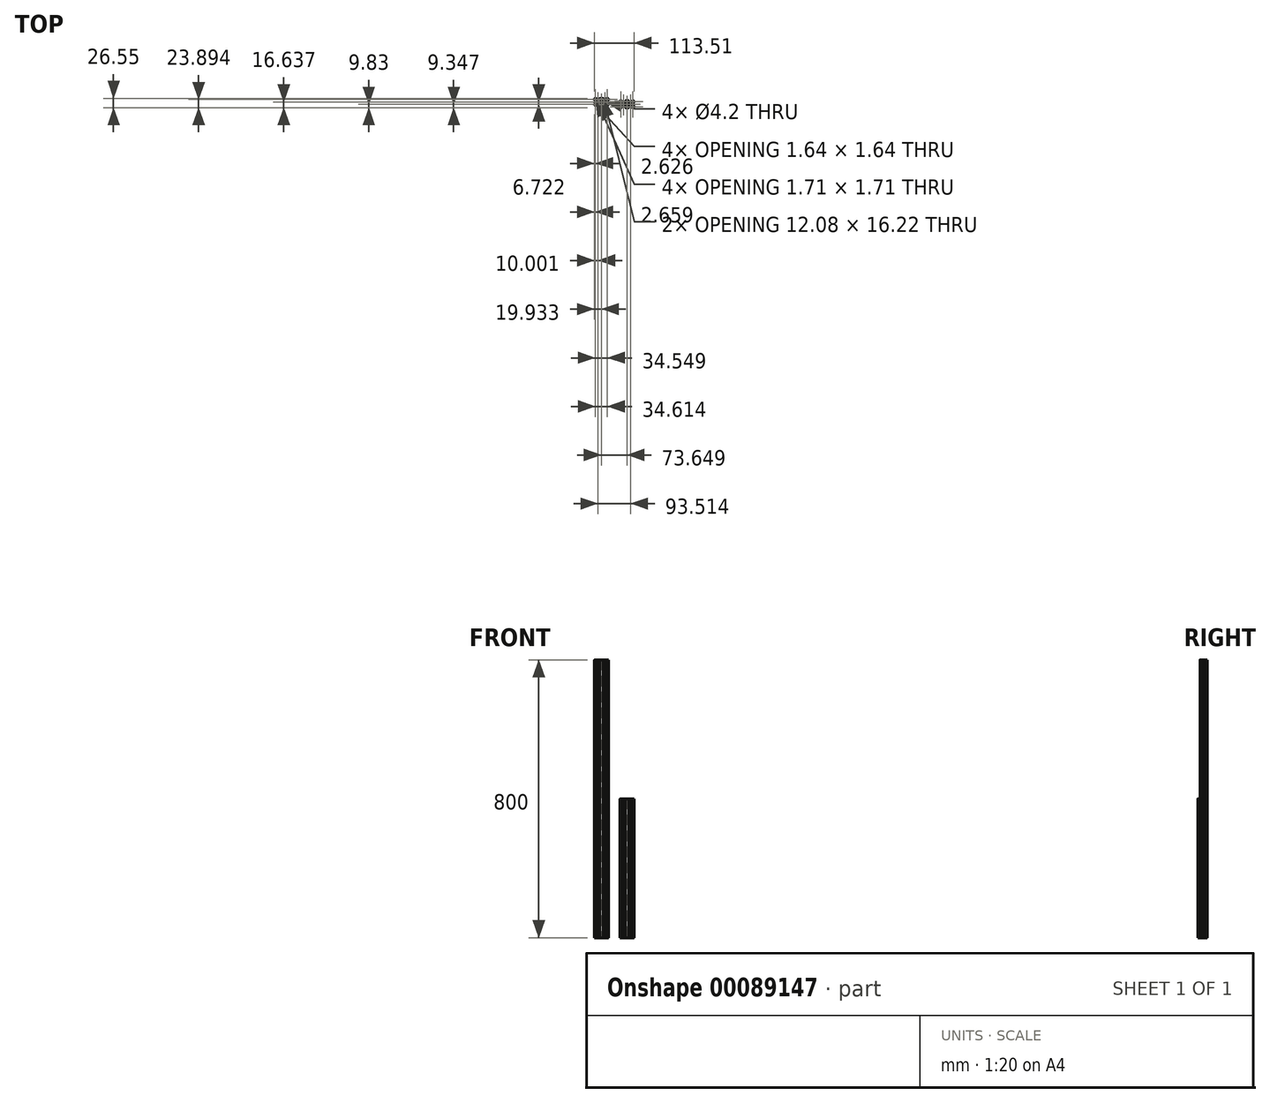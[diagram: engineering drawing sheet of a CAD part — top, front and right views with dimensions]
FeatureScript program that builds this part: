
annotation { "Feature Type Name" : "Feature", "Feature Type Description" : "" }
export const myFeature = defineFeature(function(context is Context, id is Id, definition is map)
    precondition{}
    {
        {
            var Q0;
            Q0=qCreatedBy(makeId("Top.planeOp"),FACE);
            var sketch = newSketch(context, id + "F0", { "sketchPlane" : qUnion([Q0])});
            skLineSegment(sketch, "E0.bottom", {"start": v(1.27, 0.17) * mm, "end": v(4.85, 0.17) * mm});
            skLineSegment(sketch, "E0.top", {"start": v(1.27, 20) * mm, "end": v(4.9, 20) * mm});
            skLineSegment(sketch, "E0.left", {"start": v(0, 1.44) * mm, "end": v(0, 5.01) * mm});
            skLineSegment(sketch, "E1.bottom", {"start": v(17.2, 18.2) * mm, "end": v(19.93, 18.2) * mm});
            skLineSegment(sketch, "E1.top", {"start": v(17.2, 1.97) * mm, "end": v(19.93, 1.97) * mm});
            skLineSegment(sketch, "E1.left", {"start": v(17.2, 18.2) * mm, "end": v(17.2, 16.24) * mm});
            skLineSegment(sketch, "E2.left", {"start": v(13.9, 12.92) * mm, "end": v(13.9, 7.24) * mm});
            skLineSegment(sketch, "E3", {"start": v(13.9, 12.92) * mm, "end": v(17.2, 16.24) * mm});
            skLineSegment(sketch, "E4", {"start": v(13.9, 7.24) * mm, "end": v(17.2, 3.93) * mm});
            skLineSegment(sketch, "E5.top", {"start": v(7.17, 13.95) * mm, "end": v(12.85, 13.95) * mm});
            skLineSegment(sketch, "E6", {"start": v(4.58, 18.2) * mm, "end": v(4.58, 16.55) * mm});
            skLineSegment(sketch, "E7", {"start": v(15.46, 16.56) * mm, "end": v(15.46, 18.2) * mm});
            skLineSegment(sketch, "E8", {"start": v(4.58, 16.55) * mm, "end": v(7.17, 13.95) * mm});
            skLineSegment(sketch, "E9", {"start": v(12.85, 13.95) * mm, "end": v(15.46, 16.56) * mm});
            skLineSegment(sketch, "E10", {"start": v(4.58, 18.2) * mm, "end": v(6.7, 18.2) * mm});
            skLineSegment(sketch, "E11.trimOffspring", {"start": v(17.2, 3.93) * mm, "end": v(17.2, 1.97) * mm});
            skLineSegment(sketch, "E12", {"start": v(19.93, 20) * mm, "end": v(19.93, 0.17) * mm, "construction": true});
            skLineSegment(sketch, "E13", {"start": v(1.8, 15.55) * mm, "end": v(1.8, 13.42) * mm});
            skLineSegment(sketch, "E14", {"start": v(1.8, 4.68) * mm, "end": v(3.45, 4.68) * mm});
            skLineSegment(sketch, "E15", {"start": v(3.45, 4.68) * mm, "end": v(6.05, 7.27) * mm});
            skLineSegment(sketch, "E16", {"start": v(6.05, 7.27) * mm, "end": v(6.05, 12.96) * mm});
            skLineSegment(sketch, "E17", {"start": v(6.05, 12.96) * mm, "end": v(3.45, 15.55) * mm});
            skLineSegment(sketch, "E18", {"start": v(3.45, 15.55) * mm, "end": v(1.8, 15.55) * mm});
            skLineSegment(sketch, "E19", {"start": v(7.1, 6.21) * mm, "end": v(12.8, 6.21) * mm});
            skLineSegment(sketch, "E20", {"start": v(12.8, 6.21) * mm, "end": v(15.38, 3.63) * mm});
            skLineSegment(sketch, "E21", {"start": v(15.38, 3.63) * mm, "end": v(15.38, 1.97) * mm});
            skLineSegment(sketch, "E22", {"start": v(15.38, 1.97) * mm, "end": v(13.26, 1.97) * mm});
            skLineSegment(sketch, "E23", {"start": v(4.51, 1.97) * mm, "end": v(4.51, 3.62) * mm});
            skLineSegment(sketch, "E24", {"start": v(4.51, 3.62) * mm, "end": v(7.1, 6.21) * mm});
            skLineSegment(sketch, "E25", {"start": v(1.8, 3.62) * mm, "end": v(2.34, 3.62) * mm});
            skLineSegment(sketch, "E26", {"start": v(2.34, 3.62) * mm, "end": v(3.45, 2.51) * mm});
            skLineSegment(sketch, "E27", {"start": v(3.45, 2.51) * mm, "end": v(3.45, 1.97) * mm});
            skLineSegment(sketch, "E28", {"start": v(3.45, 1.97) * mm, "end": v(1.8, 1.97) * mm});
            skLineSegment(sketch, "E29", {"start": v(1.8, 3.62) * mm, "end": v(1.8, 1.97) * mm});
            skPoint(sketch, "E30.endSnap0", {"position": v(10.01, 13.95) * mm});
            skCircle(sketch, "E31", {"center": v(10, 10) * mm, "radius": 2.1 * mm});
            skLineSegment(sketch, "E32", {"start": v(1.8, 18.2) * mm, "end": v(3.51, 18.2) * mm});
            skLineSegment(sketch, "E33", {"start": v(3.51, 18.2) * mm, "end": v(3.51, 17.66) * mm});
            skLineSegment(sketch, "E34", {"start": v(3.51, 17.66) * mm, "end": v(2.34, 16.49) * mm});
            skLineSegment(sketch, "E35", {"start": v(2.34, 16.49) * mm, "end": v(1.8, 16.49) * mm});
            skLineSegment(sketch, "E36", {"start": v(1.8, 16.49) * mm, "end": v(1.8, 18.2) * mm});
            skArc(sketch, "E37.filletArc", {"start": v(0, 1.44) * mm, "mid": v(0.37, 0.54) * mm, "end": v(1.27, 0.17) * mm});
            skArc(sketch, "E38.filletArc", {"start": v(1.27, 20) * mm, "mid": v(0.37, 19.63) * mm, "end": v(0, 18.73) * mm});
            skLineSegment(sketch, "E39", {"start": v(4.9, 20) * mm, "end": v(6.7, 18.2) * mm});
            skLineSegment(sketch, "E40", {"start": v(10.01, 13.95) * mm, "end": v(10.01, 14.9) * mm, "construction": true});
            skLineSegment(sketch, "E41", {"start": v(10.01, 14.9) * mm, "end": v(10.01, 20) * mm, "construction": true});
            skLineSegment(sketch, "E42", {"start": v(10.01, 21.22) * mm, "end": v(10.01, 20) * mm, "construction": true});
            skLineSegment(sketch, "E43.trimOffspring", {"start": v(15.12, 20) * mm, "end": v(19.93, 20) * mm});
            skLineSegment(sketch, "E44.trimOffspring", {"start": v(13.32, 18.2) * mm, "end": v(15.46, 18.2) * mm});
            skPoint(sketch, "E45.orphan", {"position": v(3.68, 21.22) * mm});
            skPoint(sketch, "E46.orphan", {"position": v(16.35, 21.22) * mm});
            skLineSegment(sketch, "E47", {"start": v(13.32, 18.2) * mm, "end": v(15.12, 20) * mm});
            skLineSegment(sketch, "E48", {"start": v(1.8, 13.42) * mm, "end": v(0, 15.22) * mm});
            skLineSegment(sketch, "E49", {"start": v(0, 5.01) * mm, "end": v(1.8, 6.82) * mm});
            skLineSegment(sketch, "E50.trimOffspring", {"start": v(0, 15.22) * mm, "end": v(0, 18.73) * mm});
            skLineSegment(sketch, "E51.trimOffspring", {"start": v(1.8, 6.82) * mm, "end": v(1.8, 4.68) * mm});
            skLineSegment(sketch, "E52", {"start": v(15.06, 0.17) * mm, "end": v(13.26, 1.97) * mm});
            skLineSegment(sketch, "E53", {"start": v(6.65, 1.97) * mm, "end": v(4.85, 0.17) * mm});
            skLineSegment(sketch, "E54.trimOffspring", {"start": v(15.06, 0.17) * mm, "end": v(19.93, 0.17) * mm});
            skLineSegment(sketch, "E55.trimOffspring", {"start": v(6.65, 1.97) * mm, "end": v(4.51, 1.97) * mm});
            skLineSegment(sketch, "E56.MirrorCS", {"start": v(36.35, 18.2) * mm, "end": v(36.35, 17.66) * mm});
            skLineSegment(sketch, "E57.MirrorCS", {"start": v(38.06, 3.62) * mm, "end": v(37.52, 3.62) * mm});
            skLineSegment(sketch, "E58.MirrorCS", {"start": v(36.42, 2.51) * mm, "end": v(36.42, 1.97) * mm});
            skLineSegment(sketch, "E59.MirrorCS", {"start": v(37.53, 16.49) * mm, "end": v(38.06, 16.49) * mm});
            skLineSegment(sketch, "E60.MirrorCS", {"start": v(29.85, 13.95) * mm, "end": v(29.85, 14.9) * mm, "construction": true});
            skLineSegment(sketch, "E61.MirrorCS", {"start": v(24.8, 0.17) * mm, "end": v(26.6, 1.97) * mm});
            skLineSegment(sketch, "E62.MirrorCS", {"start": v(35.29, 18.2) * mm, "end": v(35.29, 16.55) * mm});
            skLineSegment(sketch, "E63.MirrorCS", {"start": v(36.42, 1.97) * mm, "end": v(38.06, 1.97) * mm});
            skLineSegment(sketch, "E64.MirrorCS", {"start": v(24.48, 3.63) * mm, "end": v(24.48, 1.97) * mm});
            skLineSegment(sketch, "E65.MirrorCS", {"start": v(35.35, 1.97) * mm, "end": v(35.35, 3.62) * mm});
            skLineSegment(sketch, "E66.MirrorCS", {"start": v(22.66, 18.2) * mm, "end": v(22.66, 16.24) * mm});
            skLineSegment(sketch, "E67.MirrorCS", {"start": v(38.06, 16.49) * mm, "end": v(38.06, 18.2) * mm});
            skLineSegment(sketch, "E68.MirrorCS", {"start": v(24.4, 16.56) * mm, "end": v(24.4, 18.2) * mm});
            skLineSegment(sketch, "E69.MirrorCS", {"start": v(37.52, 3.62) * mm, "end": v(36.42, 2.51) * mm});
            skLineSegment(sketch, "E70.MirrorCS", {"start": v(38.06, 3.62) * mm, "end": v(38.06, 1.97) * mm});
            skLineSegment(sketch, "E71.MirrorCS", {"start": v(36.35, 17.66) * mm, "end": v(37.53, 16.49) * mm});
            skLineSegment(sketch, "E72.MirrorCS", {"start": v(32.76, 6.21) * mm, "end": v(27.06, 6.21) * mm});
            skLineSegment(sketch, "E73.MirrorCS", {"start": v(34.96, 20) * mm, "end": v(33.16, 18.2) * mm});
            skLineSegment(sketch, "E74.MirrorCS", {"start": v(38.06, 4.68) * mm, "end": v(36.41, 4.68) * mm});
            skLineSegment(sketch, "E75.MirrorCS", {"start": v(26.54, 18.2) * mm, "end": v(24.74, 20) * mm});
            skLineSegment(sketch, "E76.MirrorCS", {"start": v(24.74, 20) * mm, "end": v(19.93, 20) * mm});
            skLineSegment(sketch, "E77.MirrorCS", {"start": v(29.85, 14.9) * mm, "end": v(29.85, 20) * mm, "construction": true});
            skLineSegment(sketch, "E78.MirrorCS", {"start": v(33.21, 1.97) * mm, "end": v(35.02, 0.17) * mm});
            skLineSegment(sketch, "E79.MirrorCS", {"start": v(32.7, 13.95) * mm, "end": v(27.01, 13.95) * mm});
            skLineSegment(sketch, "E80.MirrorCS", {"start": v(22.66, 3.93) * mm, "end": v(22.66, 1.97) * mm});
            skLineSegment(sketch, "E81.MirrorCS", {"start": v(36.41, 4.68) * mm, "end": v(33.82, 7.27) * mm});
            skLineSegment(sketch, "E82.MirrorCS", {"start": v(29.85, 21.22) * mm, "end": v(29.85, 20) * mm, "construction": true});
            skLineSegment(sketch, "E83.MirrorCS", {"start": v(33.21, 1.97) * mm, "end": v(35.35, 1.97) * mm});
            skLineSegment(sketch, "E84.MirrorCS", {"start": v(25.97, 12.92) * mm, "end": v(25.97, 7.24) * mm});
            skLineSegment(sketch, "E85.MirrorCS", {"start": v(35.29, 18.2) * mm, "end": v(33.16, 18.2) * mm});
            skLineSegment(sketch, "E86.MirrorCS", {"start": v(27.01, 13.95) * mm, "end": v(24.4, 16.56) * mm});
            skCircle(sketch, "E87.MirrorC", {"center": v(29.86, 10) * mm, "radius": 2.1 * mm});
            skLineSegment(sketch, "E88.MirrorCS", {"start": v(38.06, 13.42) * mm, "end": v(39.86, 15.22) * mm});
            skLineSegment(sketch, "E89.MirrorCS", {"start": v(22.66, 1.97) * mm, "end": v(19.93, 1.97) * mm});
            skLineSegment(sketch, "E90.MirrorCS", {"start": v(38.6, 0.17) * mm, "end": v(35.02, 0.17) * mm});
            skLineSegment(sketch, "E91.MirrorCS", {"start": v(38.06, 18.2) * mm, "end": v(36.35, 18.2) * mm});
            skLineSegment(sketch, "E92.MirrorCS", {"start": v(33.82, 7.27) * mm, "end": v(33.82, 12.96) * mm});
            skPoint(sketch, "E93.MirrorP", {"position": v(36.18, 21.22) * mm});
            skLineSegment(sketch, "E94.MirrorCS", {"start": v(39.86, 1.44) * mm, "end": v(39.86, 5.01) * mm});
            skLineSegment(sketch, "E95.MirrorCS", {"start": v(24.48, 1.97) * mm, "end": v(26.6, 1.97) * mm});
            skLineSegment(sketch, "E96.MirrorCS", {"start": v(36.41, 15.55) * mm, "end": v(38.06, 15.55) * mm});
            skArc(sketch, "E97.MirrorCS", {"start": v(38.6, 20) * mm, "mid": v(39.5, 19.63) * mm, "end": v(39.86, 18.73) * mm});
            skPoint(sketch, "E98.MirrorP", {"position": v(29.85, 13.95) * mm});
            skPoint(sketch, "E99.MirrorP", {"position": v(23.52, 21.22) * mm});
            skLineSegment(sketch, "E100.MirrorCS", {"start": v(38.06, 6.82) * mm, "end": v(38.06, 4.68) * mm});
            skLineSegment(sketch, "E101.MirrorCS", {"start": v(24.8, 0.17) * mm, "end": v(19.93, 0.17) * mm});
            skLineSegment(sketch, "E102.MirrorCS", {"start": v(25.97, 7.24) * mm, "end": v(22.66, 3.93) * mm});
            skLineSegment(sketch, "E103.MirrorCS", {"start": v(27.06, 6.21) * mm, "end": v(24.48, 3.63) * mm});
            skLineSegment(sketch, "E104.MirrorCS", {"start": v(33.82, 12.96) * mm, "end": v(36.41, 15.55) * mm});
            skLineSegment(sketch, "E105.MirrorCS", {"start": v(35.35, 3.62) * mm, "end": v(32.76, 6.21) * mm});
            skArc(sketch, "E106.MirrorCS", {"start": v(39.86, 1.44) * mm, "mid": v(39.5, 0.54) * mm, "end": v(38.6, 0.17) * mm});
            skLineSegment(sketch, "E107.MirrorCS", {"start": v(39.86, 5.01) * mm, "end": v(38.06, 6.82) * mm});
            skLineSegment(sketch, "E108.MirrorCS", {"start": v(22.66, 18.2) * mm, "end": v(19.93, 18.2) * mm});
            skLineSegment(sketch, "E109.MirrorCS", {"start": v(38.6, 20) * mm, "end": v(34.96, 20) * mm});
            skLineSegment(sketch, "E110.MirrorCS", {"start": v(39.86, 15.22) * mm, "end": v(39.86, 18.73) * mm});
            skLineSegment(sketch, "E111.MirrorCS", {"start": v(35.29, 16.55) * mm, "end": v(32.7, 13.95) * mm});
            skLineSegment(sketch, "E112.MirrorCS", {"start": v(25.97, 12.92) * mm, "end": v(22.66, 16.24) * mm});
            skLineSegment(sketch, "E113.MirrorCS", {"start": v(26.54, 18.2) * mm, "end": v(24.4, 18.2) * mm});
            skLineSegment(sketch, "E114.MirrorCS", {"start": v(38.06, 15.55) * mm, "end": v(38.06, 13.42) * mm});
            skSolve(sketch);
        }
        {
            var Q0;
            Q0=makeQuery(id+"F0.imprint","IMPRINT",FACE,{"disambiguationData":[TD([[makeQuery(id+"F0.imprint","IMPRINT",EDGE,{"derivedFrom":sQuery(id+"F0.wireOp",EDGE,"E0.bottom")}),1.0]])]});
            extrude(context, id + "F1", {"entities" : qUnion([Q0]), "depth" : 400 * mm});
        }
        {
            var Q0;
            Q0=qCreatedBy(makeId("Top.planeOp"),FACE);
            var sketch = newSketch(context, id + "F2", { "sketchPlane" : qUnion([Q0])});
            skLineSegment(sketch, "E115.bottom", {"start": v(-72.38, 6.9) * mm, "end": v(-68.8, 6.9) * mm});
            skLineSegment(sketch, "E115.top", {"start": v(-72.38, 26.72) * mm, "end": v(-68.74, 26.72) * mm});
            skLineSegment(sketch, "E115.left", {"start": v(-73.65, 8.16) * mm, "end": v(-73.65, 11.74) * mm});
            skLineSegment(sketch, "E116.bottom", {"start": v(-56.45, 24.92) * mm, "end": v(-53.72, 24.92) * mm});
            skLineSegment(sketch, "E116.top", {"start": v(-56.45, 8.7) * mm, "end": v(-53.72, 8.7) * mm});
            skLineSegment(sketch, "E116.left", {"start": v(-56.45, 24.92) * mm, "end": v(-56.45, 22.96) * mm});
            skLineSegment(sketch, "E117.left", {"start": v(-59.76, 19.65) * mm, "end": v(-59.76, 13.97) * mm});
            skLineSegment(sketch, "E118", {"start": v(-59.76, 19.65) * mm, "end": v(-56.45, 22.96) * mm});
            skLineSegment(sketch, "E119", {"start": v(-59.76, 13.97) * mm, "end": v(-56.45, 10.66) * mm});
            skLineSegment(sketch, "E120.top", {"start": v(-66.48, 20.68) * mm, "end": v(-60.8, 20.68) * mm});
            skLineSegment(sketch, "E121", {"start": v(-69.07, 24.92) * mm, "end": v(-69.07, 23.27) * mm});
            skLineSegment(sketch, "E122", {"start": v(-58.2, 23.28) * mm, "end": v(-58.2, 24.92) * mm});
            skLineSegment(sketch, "E123", {"start": v(-69.07, 23.27) * mm, "end": v(-66.48, 20.68) * mm});
            skLineSegment(sketch, "E124", {"start": v(-60.8, 20.68) * mm, "end": v(-58.2, 23.28) * mm});
            skLineSegment(sketch, "E125", {"start": v(-69.07, 24.92) * mm, "end": v(-66.94, 24.92) * mm});
            skLineSegment(sketch, "E126.trimOffspring", {"start": v(-56.45, 10.66) * mm, "end": v(-56.45, 8.7) * mm});
            skLineSegment(sketch, "E127", {"start": v(-53.72, 26.72) * mm, "end": v(-53.72, 6.9) * mm, "construction": true});
            skLineSegment(sketch, "E128", {"start": v(-71.85, 22.28) * mm, "end": v(-71.85, 20.14) * mm});
            skLineSegment(sketch, "E129", {"start": v(-71.85, 11.4) * mm, "end": v(-70.2, 11.4) * mm});
            skLineSegment(sketch, "E130", {"start": v(-70.2, 11.4) * mm, "end": v(-67.6, 14) * mm});
            skLineSegment(sketch, "E131", {"start": v(-67.6, 14) * mm, "end": v(-67.6, 19.69) * mm});
            skLineSegment(sketch, "E132", {"start": v(-67.6, 19.69) * mm, "end": v(-70.2, 22.28) * mm});
            skLineSegment(sketch, "E133", {"start": v(-70.2, 22.28) * mm, "end": v(-71.85, 22.28) * mm});
            skLineSegment(sketch, "E134", {"start": v(-66.54, 12.94) * mm, "end": v(-60.85, 12.94) * mm});
            skLineSegment(sketch, "E135", {"start": v(-60.85, 12.94) * mm, "end": v(-58.27, 10.35) * mm});
            skLineSegment(sketch, "E136", {"start": v(-58.27, 10.35) * mm, "end": v(-58.27, 8.7) * mm});
            skLineSegment(sketch, "E137", {"start": v(-58.27, 8.7) * mm, "end": v(-60.4, 8.7) * mm});
            skLineSegment(sketch, "E138", {"start": v(-69.14, 8.7) * mm, "end": v(-69.14, 10.35) * mm});
            skLineSegment(sketch, "E139", {"start": v(-69.14, 10.35) * mm, "end": v(-66.54, 12.94) * mm});
            skLineSegment(sketch, "E140", {"start": v(-71.85, 10.34) * mm, "end": v(-71.3, 10.34) * mm});
            skLineSegment(sketch, "E141", {"start": v(-71.3, 10.34) * mm, "end": v(-70.2, 9.23) * mm});
            skLineSegment(sketch, "E142", {"start": v(-70.2, 9.23) * mm, "end": v(-70.2, 8.7) * mm});
            skLineSegment(sketch, "E143", {"start": v(-70.2, 8.7) * mm, "end": v(-71.85, 8.7) * mm});
            skLineSegment(sketch, "E144", {"start": v(-71.85, 10.34) * mm, "end": v(-71.85, 8.7) * mm});
            skPoint(sketch, "E145.endSnap0", {"position": v(-63.64, 20.68) * mm});
            skCircle(sketch, "E146", {"center": v(-63.65, 16.72) * mm, "radius": 2.1 * mm});
            skLineSegment(sketch, "E147", {"start": v(-71.85, 24.92) * mm, "end": v(-70.14, 24.92) * mm});
            skLineSegment(sketch, "E148", {"start": v(-70.14, 24.92) * mm, "end": v(-70.14, 24.39) * mm});
            skLineSegment(sketch, "E149", {"start": v(-70.14, 24.39) * mm, "end": v(-71.31, 23.2) * mm});
            skLineSegment(sketch, "E150", {"start": v(-71.31, 23.2) * mm, "end": v(-71.85, 23.2) * mm});
            skLineSegment(sketch, "E151", {"start": v(-71.85, 23.2) * mm, "end": v(-71.85, 24.92) * mm});
            skArc(sketch, "E152.filletArc", {"start": v(-73.65, 8.16) * mm, "mid": v(-73.28, 7.26) * mm, "end": v(-72.38, 6.9) * mm});
            skArc(sketch, "E153.filletArc", {"start": v(-72.38, 26.72) * mm, "mid": v(-73.28, 26.35) * mm, "end": v(-73.65, 25.45) * mm});
            skLineSegment(sketch, "E154", {"start": v(-68.74, 26.72) * mm, "end": v(-66.94, 24.92) * mm});
            skLineSegment(sketch, "E155", {"start": v(-63.64, 20.68) * mm, "end": v(-63.64, 21.61) * mm, "construction": true});
            skLineSegment(sketch, "E156", {"start": v(-63.64, 21.61) * mm, "end": v(-63.64, 26.72) * mm, "construction": true});
            skLineSegment(sketch, "E157", {"start": v(-63.64, 27.95) * mm, "end": v(-63.64, 26.72) * mm, "construction": true});
            skLineSegment(sketch, "E158.trimOffspring", {"start": v(-58.53, 26.72) * mm, "end": v(-53.72, 26.72) * mm});
            skLineSegment(sketch, "E159.trimOffspring", {"start": v(-60.33, 24.92) * mm, "end": v(-58.2, 24.92) * mm});
            skPoint(sketch, "E160.orphan", {"position": v(-69.97, 27.95) * mm});
            skPoint(sketch, "E161.orphan", {"position": v(-57.3, 27.95) * mm});
            skLineSegment(sketch, "E162", {"start": v(-60.33, 24.92) * mm, "end": v(-58.53, 26.72) * mm});
            skLineSegment(sketch, "E163", {"start": v(-71.85, 20.14) * mm, "end": v(-73.65, 21.95) * mm});
            skLineSegment(sketch, "E164", {"start": v(-73.65, 11.74) * mm, "end": v(-71.85, 13.54) * mm});
            skLineSegment(sketch, "E165.trimOffspring", {"start": v(-73.65, 21.95) * mm, "end": v(-73.65, 25.45) * mm});
            skLineSegment(sketch, "E166.trimOffspring", {"start": v(-71.85, 13.54) * mm, "end": v(-71.85, 11.4) * mm});
            skLineSegment(sketch, "E167", {"start": v(-58.6, 6.9) * mm, "end": v(-60.4, 8.7) * mm});
            skLineSegment(sketch, "E168", {"start": v(-67, 8.7) * mm, "end": v(-68.8, 6.9) * mm});
            skLineSegment(sketch, "E169.trimOffspring", {"start": v(-58.6, 6.9) * mm, "end": v(-53.72, 6.9) * mm});
            skLineSegment(sketch, "E170.trimOffspring", {"start": v(-67, 8.7) * mm, "end": v(-69.14, 8.7) * mm});
            skLineSegment(sketch, "E171.MirrorCS", {"start": v(-37.3, 24.92) * mm, "end": v(-37.3, 24.39) * mm});
            skLineSegment(sketch, "E172.MirrorCS", {"start": v(-35.59, 10.34) * mm, "end": v(-36.13, 10.34) * mm});
            skLineSegment(sketch, "E173.MirrorCS", {"start": v(-37.23, 9.23) * mm, "end": v(-37.23, 8.7) * mm});
            skLineSegment(sketch, "E174.MirrorCS", {"start": v(-36.12, 23.2) * mm, "end": v(-35.59, 23.2) * mm});
            skLineSegment(sketch, "E175.MirrorCS", {"start": v(-43.8, 20.68) * mm, "end": v(-43.8, 21.61) * mm, "construction": true});
            skLineSegment(sketch, "E176.MirrorCS", {"start": v(-48.84, 6.9) * mm, "end": v(-47.04, 8.7) * mm});
            skLineSegment(sketch, "E177.MirrorCS", {"start": v(-38.36, 24.92) * mm, "end": v(-38.36, 23.27) * mm});
            skLineSegment(sketch, "E178.MirrorCS", {"start": v(-37.23, 8.7) * mm, "end": v(-35.59, 8.7) * mm});
            skLineSegment(sketch, "E179.MirrorCS", {"start": v(-49.17, 10.35) * mm, "end": v(-49.17, 8.7) * mm});
            skLineSegment(sketch, "E180.MirrorCS", {"start": v(-38.3, 8.7) * mm, "end": v(-38.3, 10.35) * mm});
            skLineSegment(sketch, "E181.MirrorCS", {"start": v(-50.99, 24.92) * mm, "end": v(-50.99, 22.96) * mm});
            skLineSegment(sketch, "E182.MirrorCS", {"start": v(-35.59, 23.2) * mm, "end": v(-35.59, 24.92) * mm});
            skLineSegment(sketch, "E183.MirrorCS", {"start": v(-49.24, 23.28) * mm, "end": v(-49.24, 24.92) * mm});
            skLineSegment(sketch, "E184.MirrorCS", {"start": v(-36.13, 10.34) * mm, "end": v(-37.23, 9.23) * mm});
            skLineSegment(sketch, "E185.MirrorCS", {"start": v(-35.59, 10.34) * mm, "end": v(-35.59, 8.7) * mm});
            skLineSegment(sketch, "E186.MirrorCS", {"start": v(-37.3, 24.39) * mm, "end": v(-36.12, 23.2) * mm});
            skLineSegment(sketch, "E187.MirrorCS", {"start": v(-40.89, 12.94) * mm, "end": v(-46.59, 12.94) * mm});
            skLineSegment(sketch, "E188.MirrorCS", {"start": v(-38.69, 26.72) * mm, "end": v(-40.49, 24.92) * mm});
            skLineSegment(sketch, "E189.MirrorCS", {"start": v(-35.59, 11.4) * mm, "end": v(-37.24, 11.4) * mm});
            skLineSegment(sketch, "E190.MirrorCS", {"start": v(-47.1, 24.92) * mm, "end": v(-48.9, 26.72) * mm});
            skLineSegment(sketch, "E191.MirrorCS", {"start": v(-48.9, 26.72) * mm, "end": v(-53.72, 26.72) * mm});
            skLineSegment(sketch, "E192.MirrorCS", {"start": v(-43.8, 21.61) * mm, "end": v(-43.8, 26.72) * mm, "construction": true});
            skLineSegment(sketch, "E193.MirrorCS", {"start": v(-40.44, 8.7) * mm, "end": v(-38.63, 6.9) * mm});
            skLineSegment(sketch, "E194.MirrorCS", {"start": v(-40.96, 20.68) * mm, "end": v(-46.64, 20.68) * mm});
            skLineSegment(sketch, "E195.MirrorCS", {"start": v(-50.99, 10.66) * mm, "end": v(-50.99, 8.7) * mm});
            skLineSegment(sketch, "E196.MirrorCS", {"start": v(-37.24, 11.4) * mm, "end": v(-39.83, 14) * mm});
            skLineSegment(sketch, "E197.MirrorCS", {"start": v(-43.8, 27.95) * mm, "end": v(-43.8, 26.72) * mm, "construction": true});
            skLineSegment(sketch, "E198.MirrorCS", {"start": v(-40.44, 8.7) * mm, "end": v(-38.3, 8.7) * mm});
            skLineSegment(sketch, "E199.MirrorCS", {"start": v(-47.68, 19.65) * mm, "end": v(-47.68, 13.97) * mm});
            skLineSegment(sketch, "E200.MirrorCS", {"start": v(-38.36, 24.92) * mm, "end": v(-40.49, 24.92) * mm});
            skLineSegment(sketch, "E201.MirrorCS", {"start": v(-46.64, 20.68) * mm, "end": v(-49.24, 23.28) * mm});
            skCircle(sketch, "E202.MirrorC", {"center": v(-43.78, 16.72) * mm, "radius": 2.1 * mm});
            skLineSegment(sketch, "E203.MirrorCS", {"start": v(-35.59, 20.14) * mm, "end": v(-33.78, 21.95) * mm});
            skLineSegment(sketch, "E204.MirrorCS", {"start": v(-50.99, 8.7) * mm, "end": v(-53.72, 8.7) * mm});
            skLineSegment(sketch, "E205.MirrorCS", {"start": v(-35.05, 6.9) * mm, "end": v(-38.63, 6.9) * mm});
            skLineSegment(sketch, "E206.MirrorCS", {"start": v(-35.59, 24.92) * mm, "end": v(-37.3, 24.92) * mm});
            skLineSegment(sketch, "E207.MirrorCS", {"start": v(-39.83, 14) * mm, "end": v(-39.83, 19.69) * mm});
            skPoint(sketch, "E208.MirrorP", {"position": v(-37.47, 27.95) * mm});
            skLineSegment(sketch, "E209.MirrorCS", {"start": v(-33.78, 8.16) * mm, "end": v(-33.78, 11.74) * mm});
            skLineSegment(sketch, "E210.MirrorCS", {"start": v(-49.17, 8.7) * mm, "end": v(-47.04, 8.7) * mm});
            skLineSegment(sketch, "E211.MirrorCS", {"start": v(-37.24, 22.28) * mm, "end": v(-35.59, 22.28) * mm});
            skArc(sketch, "E212.MirrorCS", {"start": v(-35.05, 26.72) * mm, "mid": v(-34.16, 26.35) * mm, "end": v(-33.78, 25.45) * mm});
            skPoint(sketch, "E213.MirrorP", {"position": v(-43.8, 20.68) * mm});
            skPoint(sketch, "E214.MirrorP", {"position": v(-50.13, 27.95) * mm});
            skLineSegment(sketch, "E215.MirrorCS", {"start": v(-35.59, 13.54) * mm, "end": v(-35.59, 11.4) * mm});
            skLineSegment(sketch, "E216.MirrorCS", {"start": v(-48.84, 6.9) * mm, "end": v(-53.72, 6.9) * mm});
            skLineSegment(sketch, "E217.MirrorCS", {"start": v(-47.68, 13.97) * mm, "end": v(-50.99, 10.66) * mm});
            skLineSegment(sketch, "E218.MirrorCS", {"start": v(-46.59, 12.94) * mm, "end": v(-49.17, 10.35) * mm});
            skLineSegment(sketch, "E219.MirrorCS", {"start": v(-39.83, 19.69) * mm, "end": v(-37.24, 22.28) * mm});
            skLineSegment(sketch, "E220.MirrorCS", {"start": v(-38.3, 10.35) * mm, "end": v(-40.89, 12.94) * mm});
            skArc(sketch, "E221.MirrorCS", {"start": v(-33.78, 8.16) * mm, "mid": v(-34.16, 7.26) * mm, "end": v(-35.05, 6.9) * mm});
            skLineSegment(sketch, "E222.MirrorCS", {"start": v(-33.78, 11.74) * mm, "end": v(-35.59, 13.54) * mm});
            skLineSegment(sketch, "E223.MirrorCS", {"start": v(-50.99, 24.92) * mm, "end": v(-53.72, 24.92) * mm});
            skLineSegment(sketch, "E224.MirrorCS", {"start": v(-35.05, 26.72) * mm, "end": v(-38.69, 26.72) * mm});
            skLineSegment(sketch, "E225.MirrorCS", {"start": v(-33.78, 21.95) * mm, "end": v(-33.78, 25.45) * mm});
            skLineSegment(sketch, "E226.MirrorCS", {"start": v(-38.36, 23.27) * mm, "end": v(-40.96, 20.68) * mm});
            skLineSegment(sketch, "E227.MirrorCS", {"start": v(-47.68, 19.65) * mm, "end": v(-50.99, 22.96) * mm});
            skLineSegment(sketch, "E228.MirrorCS", {"start": v(-47.1, 24.92) * mm, "end": v(-49.24, 24.92) * mm});
            skLineSegment(sketch, "E229.MirrorCS", {"start": v(-35.59, 22.28) * mm, "end": v(-35.59, 20.14) * mm});
            skSolve(sketch);
        }
        {
            var Q0;
            Q0 = qSketchRegion(id + "F2", true);
            extrude(context, id + "F3", {"entities" : qUnion([Q0]), "depth" : 800 * mm});
        }
    });
